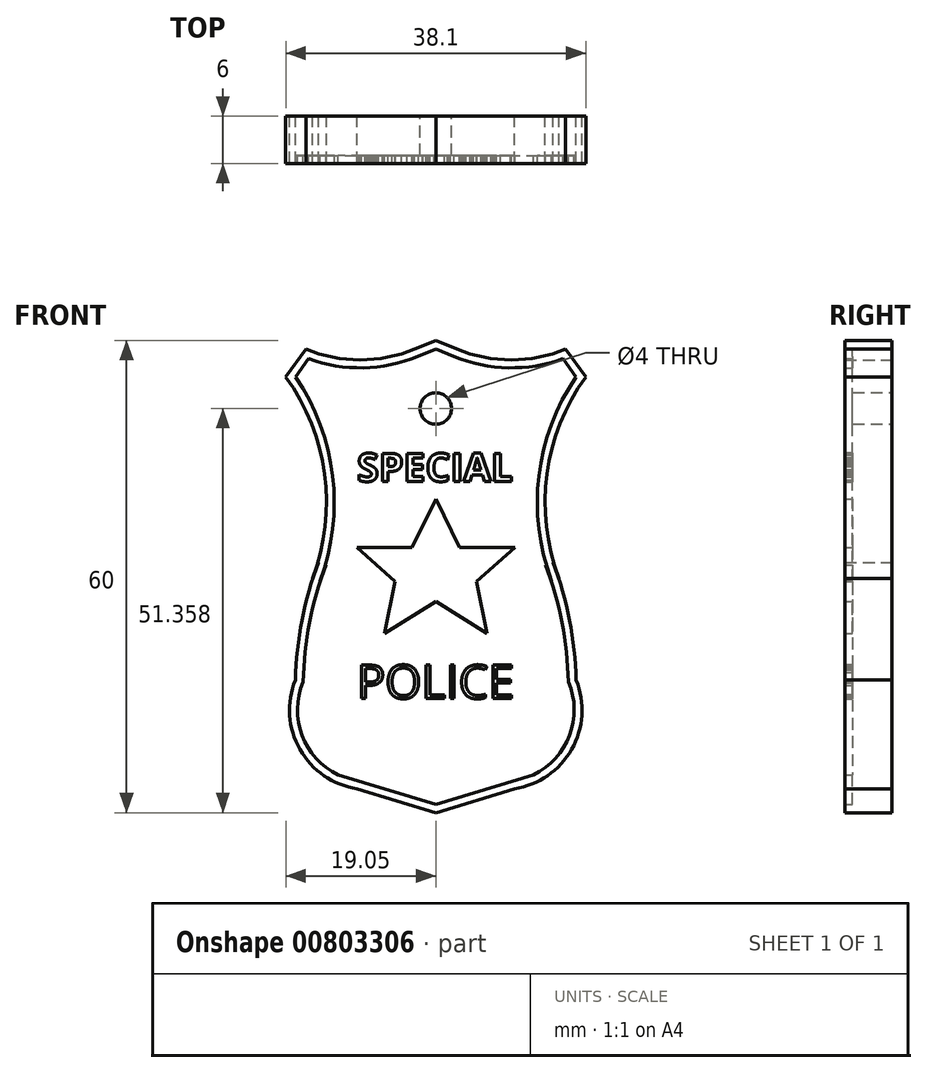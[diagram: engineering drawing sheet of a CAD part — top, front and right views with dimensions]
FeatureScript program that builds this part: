
annotation { "Feature Type Name" : "Feature", "Feature Type Description" : "" }
export const myFeature = defineFeature(function(context is Context, id is Id, definition is map)
    precondition{}
    {
        {
            var Q0;
            Q0=qCreatedBy(makeId("Front.planeOp"),FACE);
            var sketch = newSketch(context, id + "F0", { "sketchPlane" : qUnion([Q0])});
            skLineSegment(sketch, "E0", {"start": v(0, 28.18) * mm, "end": v(-2.7, 27.07) * mm});
            skArc(sketch, "E1", {"start": v(-16.5, 27.07) * mm, "mid": v(-9.6, 25.7) * mm, "end": v(-2.7, 27.07) * mm});
            skLineSegment(sketch, "E2", {"start": v(-16.5, 27.07) * mm, "end": v(-19.05, 23.56) * mm});
            skArc(sketch, "E3", {"start": v(-15.66, -2.02) * mm, "mid": v(-14.13, 11.2) * mm, "end": v(-19.05, 23.56) * mm});
            skLineSegment(sketch, "E4", {"start": v(-14.9, 0) * mm, "end": v(-15.66, -2.02) * mm});
            skArc(sketch, "E5", {"start": v(-14.9, 0) * mm, "mid": v(-17, -7.36) * mm, "end": v(-17.84, -14.96) * mm});
            skArc(sketch, "E6", {"start": v(-17.84, -14.96) * mm, "mid": v(-17.26, -23.77) * mm, "end": v(-9.98, -28.78) * mm});
            skLineSegment(sketch, "E7", {"start": v(-9.98, -28.78) * mm, "end": v(0, -31.82) * mm});
            skLineSegment(sketch, "E8.MirrorCS", {"start": v(0, 28.18) * mm, "end": v(2.7, 27.07) * mm});
            skArc(sketch, "E9.MirrorCS", {"start": v(16.5, 27.07) * mm, "mid": v(9.6, 25.7) * mm, "end": v(2.7, 27.07) * mm});
            skLineSegment(sketch, "E10.MirrorCS", {"start": v(16.5, 27.07) * mm, "end": v(19.05, 23.56) * mm});
            skArc(sketch, "E11.MirrorCS", {"start": v(15.66, -2.02) * mm, "mid": v(14.13, 11.2) * mm, "end": v(19.05, 23.56) * mm});
            skLineSegment(sketch, "E12.MirrorCS", {"start": v(14.9, 0) * mm, "end": v(15.66, -2.02) * mm});
            skArc(sketch, "E13.MirrorCS", {"start": v(14.9, 0) * mm, "mid": v(17, -7.36) * mm, "end": v(17.84, -14.96) * mm});
            skArc(sketch, "E14.MirrorCS", {"start": v(17.84, -14.96) * mm, "mid": v(17.26, -23.77) * mm, "end": v(9.98, -28.78) * mm});
            skLineSegment(sketch, "E15.MirrorCS", {"start": v(9.98, -28.78) * mm, "end": v(0, -31.82) * mm});
            skText(sketch, "E16", { "text": "SPECIAL", "fontName": "OpenSans-Bold.ttf"});
            skText(sketch, "E17", { "text": "POLICE", "fontName": "OpenSans-Regular.ttf"});
            skCircle(sketch, "E18", {"center": v(0, 19.54) * mm, "radius": 2 * mm});
            skLineSegment(sketch, "E19.0", {"start": v(-16.15, 25.86) * mm, "end": v(-17.82, 23.55) * mm});
            skArc(sketch, "E19.1", {"start": v(-14.72, -2.38) * mm, "mid": v(-13.1, 10.97) * mm, "end": v(-17.82, 23.55) * mm});
            skLineSegment(sketch, "E19.2", {"start": v(-13.96, -0.35) * mm, "end": v(-14.72, -2.38) * mm});
            skArc(sketch, "E19.3", {"start": v(-13.96, -0.35) * mm, "mid": v(-16.03, -7.64) * mm, "end": v(-16.84, -15.18) * mm});
            skArc(sketch, "E19.4", {"start": v(-16.84, -15.18) * mm, "mid": v(-17, -21.98) * mm, "end": v(-12.4, -27) * mm});
            skLineSegment(sketch, "E19.5", {"start": v(16.15, 25.86) * mm, "end": v(17.82, 23.55) * mm});
            skArc(sketch, "E19.6", {"start": v(16.15, 25.86) * mm, "mid": v(9.2, 24.7) * mm, "end": v(2.32, 26.15) * mm});
            skLineSegment(sketch, "E19.7", {"start": v(0, 27.1) * mm, "end": v(2.32, 26.15) * mm});
            skLineSegment(sketch, "E19.8", {"start": v(0, 27.1) * mm, "end": v(-2.32, 26.15) * mm});
            skArc(sketch, "E19.9", {"start": v(14.72, -2.38) * mm, "mid": v(13.1, 10.97) * mm, "end": v(17.82, 23.55) * mm});
            skLineSegment(sketch, "E19.10", {"start": v(13.96, -0.35) * mm, "end": v(14.72, -2.38) * mm});
            skArc(sketch, "E19.11", {"start": v(13.96, -0.35) * mm, "mid": v(16.03, -7.64) * mm, "end": v(16.84, -15.18) * mm});
            skArc(sketch, "E19.12", {"start": v(16.84, -15.18) * mm, "mid": v(17, -21.98) * mm, "end": v(12.4, -27) * mm});
            skLineSegment(sketch, "E19.13", {"start": v(12.4, -27) * mm, "end": v(0, -30.77) * mm});
            skArc(sketch, "E19.14", {"start": v(-16.15, 25.86) * mm, "mid": v(-9.2, 24.7) * mm, "end": v(-2.32, 26.15) * mm});
            skLineSegment(sketch, "E19.15", {"start": v(-12.4, -27) * mm, "end": v(0, -30.77) * mm});
            skLineSegment(sketch, "E20.0", {"start": v(0, 8.05) * mm, "end": v(-3, 1.86) * mm});
            skLineSegment(sketch, "E20.1", {"start": v(0, 8.05) * mm, "end": v(3, 1.86) * mm});
            skLineSegment(sketch, "E20.2", {"start": v(-3, 1.86) * mm, "end": v(-10.04, 1.86) * mm});
            skLineSegment(sketch, "E20.3", {"start": v(3, 1.86) * mm, "end": v(10.04, 1.86) * mm});
            skLineSegment(sketch, "E20.4", {"start": v(10.04, 1.86) * mm, "end": v(5.17, -2.42) * mm});
            skLineSegment(sketch, "E20.5", {"start": v(5.17, -2.42) * mm, "end": v(6.5, -9) * mm});
            skLineSegment(sketch, "E20.6", {"start": v(-10.04, 1.86) * mm, "end": v(-5.17, -2.42) * mm});
            skLineSegment(sketch, "E20.7", {"start": v(-5.17, -2.42) * mm, "end": v(-6.5, -9) * mm});
            skLineSegment(sketch, "E20.8", {"start": v(-6.5, -9) * mm, "end": v(0, -4.95) * mm});
            skLineSegment(sketch, "E20.9", {"start": v(6.5, -9) * mm, "end": v(0, -4.95) * mm});
            const initialGuessF0  = {"E16": [-0.01, 0.01027, 1, 0, 0.0036], "E17": [-0.01, -0.0173, 1, 0, 0.00427]};
            skSetInitialGuess(sketch, initialGuessF0);
            skSolve(sketch);
        }
        {
            var Q0;
            Q0=makeQuery(id+"F0.imprint","IMPRINT",FACE,{"disambiguationData":[TD([[makeQuery(id+"F0.imprint","IMPRINT",EDGE,{"derivedFrom":sQuery(id+"F0.wireOp",EDGE,"E0")}),1.0]])]});
            var Q1;
            Q1=makeQuery(id+"F0.imprint","IMPRINT",FACE,{"disambiguationData":[TD([[makeQuery(id+"F0.imprint","IMPRINT",EDGE,{"derivedFrom":sQuery(id+"F0.wireOp",EDGE,"E17.sketch_text.stroke-23")}),1.0]])]});
            var Q2;
            Q2=makeQuery(id+"F0.imprint","IMPRINT",FACE,{"disambiguationData":[TD([[makeQuery(id+"F0.imprint","IMPRINT",EDGE,{"derivedFrom":sQuery(id+"F0.wireOp",EDGE,"E17.sketch_text.stroke-8")}),1.0]])]});
            var Q3;
            Q3=makeQuery(id+"F0.imprint","IMPRINT",FACE,{"disambiguationData":[TD([[makeQuery(id+"F0.imprint","IMPRINT",EDGE,{"derivedFrom":sQuery(id+"F0.wireOp",EDGE,"E16.sketch_text.stroke-33")}),1.0]])]});
            var Q4;
            Q4=makeQuery(id+"F0.imprint","IMPRINT",FACE,{"disambiguationData":[TD([[makeQuery(id+"F0.imprint","IMPRINT",EDGE,{"derivedFrom":sQuery(id+"F0.wireOp",EDGE,"E16.sketch_text.stroke-79")}),1.0]])]});
            var Q5;
            Q5=makeQuery(id+"F0.imprint","IMPRINT",FACE,{"disambiguationData":[TD([[makeQuery(id+"F0.imprint","IMPRINT",EDGE,{"derivedFrom":sQuery(id+"F0.wireOp",EDGE,"E16.sketch_text.stroke-83")}),1.0]])]});
            extrude(context, id + "F1", {"entities" : qUnion([Q0, Q1, Q2, Q3, Q4, Q5]), "depth" : 5 * mm, "offsetDistance" : 25 * mm});
        }
        {
            var Q0;
            Q0=makeQuery(id+"F0.imprint","IMPRINT",FACE,{"disambiguationData":[TD([[makeQuery(id+"F0.imprint","IMPRINT",EDGE,{"derivedFrom":sQuery(id+"F0.wireOp",EDGE,"E16.sketch_text.stroke-52")}),-1.0]])]});
            var Q1;
            Q1=makeQuery(id+"F0.imprint","IMPRINT",FACE,{"disambiguationData":[TD([[makeQuery(id+"F0.imprint","IMPRINT",EDGE,{"derivedFrom":sQuery(id+"F0.wireOp",EDGE,"E16.sketch_text.stroke-67")}),-1.0]])]});
            var Q2;
            Q2=makeQuery(id+"F0.imprint","IMPRINT",FACE,{"disambiguationData":[TD([[makeQuery(id+"F0.imprint","IMPRINT",EDGE,{"derivedFrom":sQuery(id+"F0.wireOp",EDGE,"E16.sketch_text.stroke-71")}),-1.0]])]});
            var Q3;
            Q3=makeQuery(id+"F0.imprint","IMPRINT",FACE,{"disambiguationData":[TD([[makeQuery(id+"F0.imprint","IMPRINT",EDGE,{"derivedFrom":sQuery(id+"F0.wireOp",EDGE,"E16.sketch_text.stroke-84")}),-1.0]])]});
            var Q4;
            Q4=makeQuery(id+"F0.imprint","IMPRINT",FACE,{"disambiguationData":[TD([[makeQuery(id+"F0.imprint","IMPRINT",EDGE,{"derivedFrom":sQuery(id+"F0.wireOp",EDGE,"E16.sketch_text.stroke-40")}),-1.0]])]});
            var Q5;
            Q5=makeQuery(id+"F0.imprint","IMPRINT",FACE,{"disambiguationData":[TD([[makeQuery(id+"F0.imprint","IMPRINT",EDGE,{"derivedFrom":sQuery(id+"F0.wireOp",EDGE,"E16.sketch_text.stroke-25")}),-1.0]])]});
            var Q6;
            Q6=makeQuery(id+"F0.imprint","IMPRINT",FACE,{"disambiguationData":[TD([[makeQuery(id+"F0.imprint","IMPRINT",EDGE,{"derivedFrom":sQuery(id+"F0.wireOp",EDGE,"E16.sketch_text.stroke-0")}),-1.0]])]});
            var Q7;
            Q7=makeQuery(id+"F0.imprint","IMPRINT",FACE,{"disambiguationData":[TD([[makeQuery(id+"F0.imprint","IMPRINT",EDGE,{"derivedFrom":sQuery(id+"F0.wireOp",EDGE,"E17.sketch_text.stroke-0")}),-1.0]])]});
            var Q8;
            Q8=makeQuery(id+"F0.imprint","IMPRINT",FACE,{"disambiguationData":[TD([[makeQuery(id+"F0.imprint","IMPRINT",EDGE,{"derivedFrom":sQuery(id+"F0.wireOp",EDGE,"E17.sketch_text.stroke-15")}),-1.0]])]});
            var Q9;
            Q9=makeQuery(id+"F0.imprint","IMPRINT",FACE,{"disambiguationData":[TD([[makeQuery(id+"F0.imprint","IMPRINT",EDGE,{"derivedFrom":sQuery(id+"F0.wireOp",EDGE,"E17.sketch_text.stroke-31")}),-1.0]])]});
            var Q10;
            Q10=makeQuery(id+"F0.imprint","IMPRINT",FACE,{"disambiguationData":[TD([[makeQuery(id+"F0.imprint","IMPRINT",EDGE,{"derivedFrom":sQuery(id+"F0.wireOp",EDGE,"E17.sketch_text.stroke-37")}),-1.0]])]});
            var Q11;
            Q11=makeQuery(id+"F0.imprint","IMPRINT",FACE,{"disambiguationData":[TD([[makeQuery(id+"F0.imprint","IMPRINT",EDGE,{"derivedFrom":sQuery(id+"F0.wireOp",EDGE,"E17.sketch_text.stroke-41")}),-1.0]])]});
            var Q12;
            Q12=makeQuery(id+"F0.imprint","IMPRINT",FACE,{"disambiguationData":[TD([[makeQuery(id+"F0.imprint","IMPRINT",EDGE,{"derivedFrom":sQuery(id+"F0.wireOp",EDGE,"E17.sketch_text.stroke-56")}),-1.0]])]});
            var Q13;
            Q13=makeQuery(id+"F0.imprint","IMPRINT",FACE,{"disambiguationData":[TD([[makeQuery(id+"F0.imprint","IMPRINT",EDGE,{"derivedFrom":sQuery(id+"F0.wireOp",EDGE,"NOtKyspK-aMgI-E213-jnYd-Em1mE4TUm0l8")}),1.0]])]});
            var Q14;
            Q14=makeQuery(id+"F0.imprint","IMPRINT",FACE,{"disambiguationData":[TD([[makeQuery(id+"F0.imprint","IMPRINT",EDGE,{"derivedFrom":sQuery(id+"F0.wireOp",EDGE,"E20.0")}),1.0]])]});
            var Q15;
            Q15=makeQuery(id+"F0.imprint","IMPRINT",FACE,{"disambiguationData":[TD([[makeQuery(id+"F0.imprint","IMPRINT",EDGE,{"derivedFrom":sQuery(id+"F0.wireOp",EDGE,"E0")}),1.0]])]});
            var Q16;
            Q16=makeQuery(id+"F0.imprint","IMPRINT",FACE,{"disambiguationData":[TD([[makeQuery(id+"F0.imprint","IMPRINT",EDGE,{"derivedFrom":sQuery(id+"F0.wireOp",EDGE,"E16.sketch_text.stroke-87")}),-1.0]])]});
            extrude(context, id + "F2", {"entities" : qUnion([Q0, Q1, Q2, Q3, Q4, Q5, Q6, Q7, Q8, Q9, Q10, Q11, Q12, Q13, Q14, Q15, Q16]), "operationType" : NewBodyOperationType.ADD, "depth" : 6 * mm, "offsetDistance" : 25 * mm});
        }
    });
